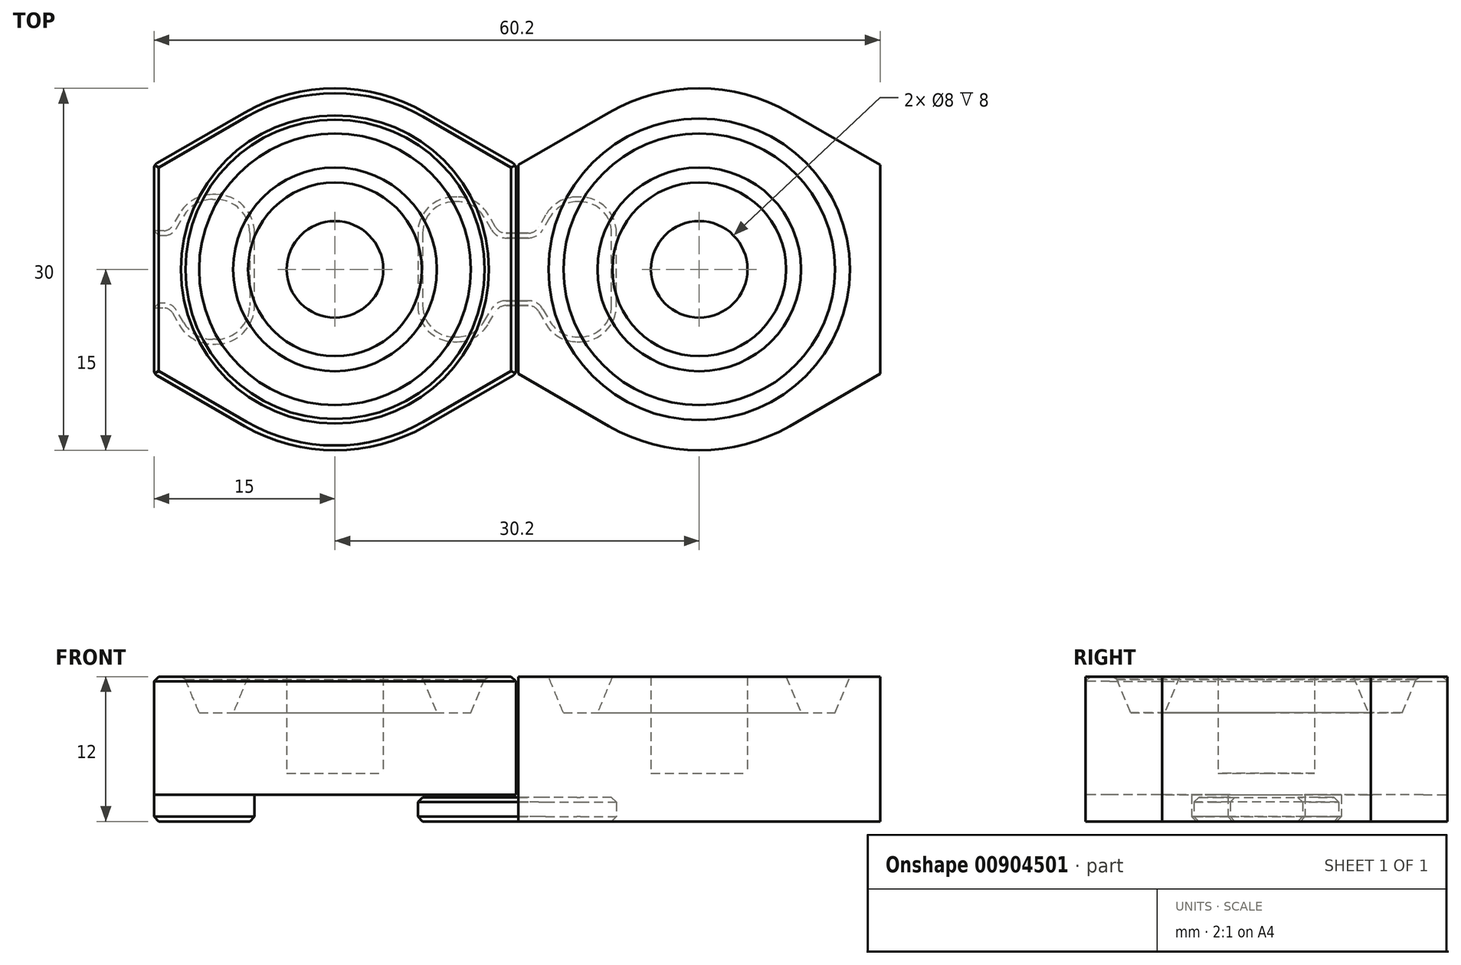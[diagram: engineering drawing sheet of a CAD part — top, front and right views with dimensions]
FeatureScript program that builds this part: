
annotation { "Feature Type Name" : "Feature", "Feature Type Description" : "" }
export const myFeature = defineFeature(function(context is Context, id is Id, definition is map)
    precondition{}
    {
        {
            var Q0;
            Q0=qCreatedBy(makeId("Front.planeOp"),FACE);
            var sketch = newSketch(context, id + "F0", { "sketchPlane" : qUnion([Q0])});
            skLineSegment(sketch, "E0", {"start": v(0, 0) * mm, "end": v(0, 53.45) * mm});
            skLineSegment(sketch, "E1", {"start": v(-4, 12) * mm, "end": v(-7.2, 12) * mm});
            skLineSegment(sketch, "E2", {"start": v(-7.2, 12) * mm, "end": v(-8.44, 9) * mm});
            skLineSegment(sketch, "E3", {"start": v(-8.44, 9) * mm, "end": v(-11.26, 9) * mm});
            skLineSegment(sketch, "E4", {"start": v(-11.26, 9) * mm, "end": v(-12.5, 12) * mm});
            skLineSegment(sketch, "E5", {"start": v(-12.5, 12) * mm, "end": v(-15, 12) * mm});
            skLineSegment(sketch, "E6", {"start": v(-15, 12) * mm, "end": v(-15, 0) * mm});
            skLineSegment(sketch, "E7", {"start": v(-15, 0) * mm, "end": v(0, 0) * mm});
            skLineSegment(sketch, "E8", {"start": v(-4, 12) * mm, "end": v(-4, 0) * mm});
            skLineSegment(sketch, "E9", {"start": v(-9.85, 9) * mm, "end": v(-9.85, 22.32) * mm});
            skLineSegment(sketch, "E10", {"start": v(-4, 4) * mm, "end": v(0, 4) * mm});
            skSolve(sketch);
        }
        {
            var Q0;
            {var subQ4=sQuery(id+"F0.wireOp",EDGE,"E1");Q0=makeQuery(id+"F0.imprint","IMPRINT",FACE,{"disambiguationData":[TD([[makeQuery(id+"F0.imprint","IMPRINT",EDGE,{"derivedFrom":subQ4}),1.0]])]});}
            var Q1;
            {var subQ3=sQuery(id+"F0.wireOp",EDGE,"E10");Q1=makeQuery(id+"F0.imprint","IMPRINT",FACE,{"disambiguationData":[TD([[makeQuery(id+"F0.imprint","IMPRINT",EDGE,{"derivedFrom":subQ3}),-1.0]])]});}
            var Q2;
            Q2=sQuery(id+"F0.wireOp",EDGE,"E0");
            revolve(context, id + "F1", {"surfaceOperationType" : NewSurfaceOperationType.NEW, "entities" : qUnion([Q0, Q1]), "axis" : qUnion([Q2]), "revolveType" : RevolveType.FULL});
        }
        {
            var Q0;
            Q0=qCreatedBy(makeId("Top.planeOp"),FACE);
            var sketch = newSketch(context, id + "F2", { "sketchPlane" : qUnion([Q0])});
            skCircle(sketch, "E11.cCircle", {"center": v(0, 0) * mm, "radius": 15 * mm, "construction": true});
            skLineSegment(sketch, "E11.0", {"start": v(-15, -8.66) * mm, "end": v(-15, 8.66) * mm});
            skLineSegment(sketch, "E11.1", {"start": v(-15, 8.66) * mm, "end": v(0, 17.32) * mm});
            skLineSegment(sketch, "E11.2", {"start": v(0, 17.32) * mm, "end": v(15, 8.66) * mm});
            skLineSegment(sketch, "E11.3", {"start": v(15, 8.66) * mm, "end": v(15, -8.66) * mm});
            skLineSegment(sketch, "E11.4", {"start": v(15, -8.66) * mm, "end": v(0, -17.32) * mm});
            skLineSegment(sketch, "E11.5", {"start": v(0, -17.32) * mm, "end": v(-15, -8.66) * mm});
            skPoint(sketch, "E11.0.midPoint", {"position": v(-15, 0) * mm});
            skCircle(sketch, "E12.0.0", {"center": v(0, 0) * mm, "radius": 15 * mm});
            skSolve(sketch);
        }
        {
            var Q0;
            {var subQ0=sQuery(id+"F2.wireOp",EDGE,"E11.1");var subQ1=sQuery(id+"F2.wireOp",EDGE,"E11.0");var subQ2=makeQuery(id+"F2.imprint","INTERSECT",VERTEX,{"derivedFrom":[subQ1,subQ0]});Q0=makeQuery(id+"F2.imprint","IMPRINT",FACE,{"disambiguationData":[TD([[makeQuery(id+"F2.imprint","IMPRINT",EDGE,{"disambiguationData":[TD([[subQ2,1.0]])],"derivedFrom":subQ1}),-1.0]])]});}
            var Q1;
            {var subQ0=sQuery(id+"F2.wireOp",EDGE,"E11.5");var subQ1=sQuery(id+"F2.wireOp",EDGE,"E11.0");var subQ2=makeQuery(id+"F2.imprint","INTERSECT",VERTEX,{"derivedFrom":[subQ1,subQ0]});Q1=makeQuery(id+"F2.imprint","IMPRINT",FACE,{"disambiguationData":[TD([[makeQuery(id+"F2.imprint","IMPRINT",EDGE,{"disambiguationData":[TD([[subQ2,-1.0]])],"derivedFrom":subQ1}),-1.0]])]});}
            var Q2;
            {var subQ0=sQuery(id+"F2.wireOp",EDGE,"E11.4");var subQ1=sQuery(id+"F2.wireOp",EDGE,"E11.3");var subQ2=makeQuery(id+"F2.imprint","INTERSECT",VERTEX,{"derivedFrom":[subQ1,subQ0]});Q2=makeQuery(id+"F2.imprint","IMPRINT",FACE,{"disambiguationData":[TD([[makeQuery(id+"F2.imprint","IMPRINT",EDGE,{"disambiguationData":[TD([[subQ2,1.0]])],"derivedFrom":subQ1}),-1.0]])]});}
            var Q3;
            {var subQ0=sQuery(id+"F2.wireOp",EDGE,"E11.3");var subQ1=sQuery(id+"F2.wireOp",EDGE,"E11.2");var subQ2=makeQuery(id+"F2.imprint","INTERSECT",VERTEX,{"derivedFrom":[subQ1,subQ0]});Q3=makeQuery(id+"F2.imprint","IMPRINT",FACE,{"disambiguationData":[TD([[makeQuery(id+"F2.imprint","IMPRINT",EDGE,{"disambiguationData":[TD([[subQ2,1.0]])],"derivedFrom":subQ1}),-1.0]])]});}
            var Q4;
            Q4=makeQuery(id+"F1.opRevolve","SWEPT_FACE",FACE,{"disambiguationData":[OSD([sQuery(id+"F0.wireOp",EDGE,"E5")])]});
            extrude(context, id + "F3", {"entities" : qUnion([Q0, Q1, Q2, Q3]), "operationType" : NewBodyOperationType.ADD, "endBound" : BoundingType.UP_TO_SURFACE, "depth" : 25 * mm, "endBoundEntityFace" : qUnion([Q4]), "offsetDistance" : 25 * mm});
        }
        {
            var Q0;
            Q0=makeQuery(id+"F1.opRevolve","SWEPT_BODY",BODY,{"disambiguationData":[OSD([sQuery(id+"F0.wireOp",EDGE,"E0"),sQuery(id+"F0.wireOp",EDGE,"E1"),sQuery(id+"F0.wireOp",EDGE,"E2"),sQuery(id+"F0.wireOp",EDGE,"E3"),sQuery(id+"F0.wireOp",EDGE,"E4"),sQuery(id+"F0.wireOp",EDGE,"E5"),sQuery(id+"F0.wireOp",EDGE,"E6"),sQuery(id+"F0.wireOp",EDGE,"E7"),sQuery(id+"F0.wireOp",EDGE,"E8"),sQuery(id+"F0.wireOp",EDGE,"E10")])]});
            transform(context, id + "F4", {"entities" : qUnion([Q0]), "transformType" : TransformType.TRANSLATION_3D, "dx" : 30.2 * mm, "dy" : 0 * mm, "dz" : 0 * mm, "makeCopy" : true});
        }
        {
            var Q0;
            {var subQ0=sQuery(id+"F2.wireOp",EDGE,"E12.0.0");var subQ1=sQuery(id+"F2.wireOp",EDGE,"E11.3");var subQ2=sQuery(id+"F2.wireOp",EDGE,"E11.0");Q0=makeQuery(id+"F3.boolean.opBoolean","MERGE",FACE,{"derivedFrom":[makeQuery(id+"F1.opRevolve","SWEPT_FACE",FACE,{"disambiguationData":[OSD([sQuery(id+"F0.wireOp",EDGE,"E7")])]}),makeQuery(id+"F3.opExtrude","CAP_FACE",FACE,{"disambiguationData":[OSD([subQ2,sQuery(id+"F2.wireOp",EDGE,"E11.5"),subQ0])],"isStart":true}),makeQuery(id+"F3.opExtrude","CAP_FACE",FACE,{"disambiguationData":[OSD([subQ2,sQuery(id+"F2.wireOp",EDGE,"E11.1"),subQ0])],"isStart":true}),makeQuery(id+"F3.opExtrude","CAP_FACE",FACE,{"disambiguationData":[OSD([sQuery(id+"F2.wireOp",EDGE,"E11.2"),subQ1,subQ0])],"isStart":true}),makeQuery(id+"F3.opExtrude","CAP_FACE",FACE,{"disambiguationData":[OSD([subQ1,sQuery(id+"F2.wireOp",EDGE,"E11.4"),subQ0])],"isStart":true})]});}
            var sketch = newSketch(context, id + "F5", { "sketchPlane" : qUnion([Q0])});
            skLineSegment(sketch, "E13", {"start": v(15, 3) * mm, "end": v(14.18, 3) * mm});
            skLineSegment(sketch, "E14", {"start": v(13.31, 3.5) * mm, "end": v(12.73, 4.5) * mm});
            skLineSegment(sketch, "E15", {"start": v(10.14, 6) * mm, "end": v(9.87, 6) * mm});
            skLineSegment(sketch, "E16", {"start": v(6.87, 3) * mm, "end": v(6.87, -3) * mm});
            skLineSegment(sketch, "E17", {"start": v(9.87, -6) * mm, "end": v(10.14, -6) * mm});
            skLineSegment(sketch, "E18", {"start": v(12.73, -4.5) * mm, "end": v(13.31, -3.5) * mm});
            skLineSegment(sketch, "E19", {"start": v(14.18, -3) * mm, "end": v(15, -3) * mm});
            skLineSegment(sketch, "E20", {"start": v(15, -3) * mm, "end": v(15.1, -3) * mm});
            skLineSegment(sketch, "E21", {"start": v(15.1, -3) * mm, "end": v(15.1, 3) * mm});
            skLineSegment(sketch, "E22", {"start": v(15.1, 3) * mm, "end": v(15, 3) * mm});
            skPoint(sketch, "E23.visualSharp", {"position": v(6.87, 6) * mm});
            skArc(sketch, "E23.filletArc", {"start": v(9.87, 6) * mm, "mid": v(7.75, 5.12) * mm, "end": v(6.87, 3) * mm});
            skPoint(sketch, "E24.visualSharp", {"position": v(6.87, -6) * mm});
            skArc(sketch, "E24.filletArc", {"start": v(6.87, -3) * mm, "mid": v(7.75, -5.12) * mm, "end": v(9.87, -6) * mm});
            skPoint(sketch, "E25.visualSharp", {"position": v(11.87, -6) * mm});
            skArc(sketch, "E25.filletArc", {"start": v(10.14, -6) * mm, "mid": v(11.64, -5.6) * mm, "end": v(12.73, -4.5) * mm});
            skPoint(sketch, "E26.visualSharp", {"position": v(11.87, 6) * mm});
            skArc(sketch, "E26.filletArc", {"start": v(12.73, 4.5) * mm, "mid": v(11.64, 5.6) * mm, "end": v(10.14, 6) * mm});
            skPoint(sketch, "E27.visualSharp", {"position": v(13.6, 3) * mm});
            skArc(sketch, "E27.filletArc", {"start": v(13.31, 3.5) * mm, "mid": v(13.68, 3.13) * mm, "end": v(14.18, 3) * mm});
            skPoint(sketch, "E28.visualSharp", {"position": v(13.6, -3) * mm});
            skArc(sketch, "E28.filletArc", {"start": v(14.18, -3) * mm, "mid": v(13.68, -3.13) * mm, "end": v(13.31, -3.5) * mm});
            skLineSegment(sketch, "E29.MirrorCS", {"start": v(15.1, 3) * mm, "end": v(15.2, 3) * mm});
            skLineSegment(sketch, "E30.MirrorCS", {"start": v(15.2, -3) * mm, "end": v(15.1, -3) * mm});
            skLineSegment(sketch, "E31.MirrorCS", {"start": v(20.33, -6) * mm, "end": v(20.06, -6) * mm});
            skLineSegment(sketch, "E32.MirrorCS", {"start": v(20.06, 6) * mm, "end": v(20.33, 6) * mm});
            skArc(sketch, "E33.MirrorCS", {"start": v(16.89, 3.5) * mm, "mid": v(16.52, 3.13) * mm, "end": v(16.02, 3) * mm});
            skArc(sketch, "E34.MirrorCS", {"start": v(16.02, -3) * mm, "mid": v(16.52, -3.13) * mm, "end": v(16.89, -3.5) * mm});
            skPoint(sketch, "E35.MirrorP", {"position": v(18.33, -6) * mm});
            skLineSegment(sketch, "E36.MirrorCS", {"start": v(16.89, 3.5) * mm, "end": v(17.47, 4.5) * mm});
            skPoint(sketch, "E37.MirrorP", {"position": v(18.33, 6) * mm});
            skPoint(sketch, "E38.MirrorP", {"position": v(23.33, 6) * mm});
            skPoint(sketch, "E39.MirrorP", {"position": v(16.6, -3) * mm});
            skArc(sketch, "E40.MirrorCS", {"start": v(23.33, -3) * mm, "mid": v(22.45, -5.12) * mm, "end": v(20.33, -6) * mm});
            skPoint(sketch, "E41.MirrorP", {"position": v(16.6, 3) * mm});
            skArc(sketch, "E42.MirrorCS", {"start": v(17.47, 4.5) * mm, "mid": v(18.56, 5.6) * mm, "end": v(20.06, 6) * mm});
            skArc(sketch, "E43.MirrorCS", {"start": v(20.33, 6) * mm, "mid": v(22.45, 5.12) * mm, "end": v(23.33, 3) * mm});
            skLineSegment(sketch, "E44.MirrorCS", {"start": v(17.47, -4.5) * mm, "end": v(16.89, -3.5) * mm});
            skLineSegment(sketch, "E45.MirrorCS", {"start": v(23.33, 3) * mm, "end": v(23.33, -3) * mm});
            skLineSegment(sketch, "E46.MirrorCS", {"start": v(15.2, 3) * mm, "end": v(16.02, 3) * mm});
            skPoint(sketch, "E47.MirrorP", {"position": v(23.33, -6) * mm});
            skLineSegment(sketch, "E48.MirrorCS", {"start": v(16.02, -3) * mm, "end": v(15.2, -3) * mm});
            skArc(sketch, "E49.MirrorCS", {"start": v(20.06, -6) * mm, "mid": v(18.56, -5.6) * mm, "end": v(17.47, -4.5) * mm});
            skSolve(sketch);
        }
        {
            var Q0;
            {var subQ1=sQuery(id+"F5.wireOp",EDGE,"E13");Q0=makeQuery(id+"F5.imprint","IMPRINT",FACE,{"disambiguationData":[TD([[makeQuery(id+"F5.imprint","IMPRINT",EDGE,{"derivedFrom":subQ1}),1.0]])]});}
            var Q1;
            {var subQ0=sQuery(id+"F5.wireOp",EDGE,"E20");Q1=makeQuery(id+"F5.imprint","IMPRINT",FACE,{"disambiguationData":[TD([[makeQuery(id+"F5.imprint","IMPRINT",EDGE,{"derivedFrom":subQ0}),1.0]])]});}
            var Q2;
            Q2=makeQuery(id+"F5.imprint","IMPRINT",FACE,{"disambiguationData":[TD([[makeQuery(id+"F5.imprint","IMPRINT",EDGE,{"derivedFrom":sQuery(id+"F5.wireOp",EDGE,"E21")}),-1.0]])]});
            extrude(context, id + "F6", {"entities" : qUnion([Q0, Q1, Q2]), "oppositeDirection" : true, "depth" : 2 * mm, "offsetDistance" : 25 * mm});
        }
        {
            var Q0;
            Q0=makeQuery(id+"F6.opExtrude","SWEPT_BODY",BODY,{"disambiguationData":[OSD([sQuery(id+"F5.wireOp",EDGE,"E13"),sQuery(id+"F5.wireOp",EDGE,"E14"),sQuery(id+"F5.wireOp",EDGE,"E15"),sQuery(id+"F5.wireOp",EDGE,"E16"),sQuery(id+"F5.wireOp",EDGE,"E17"),sQuery(id+"F5.wireOp",EDGE,"E18"),sQuery(id+"F5.wireOp",EDGE,"E19"),sQuery(id+"F5.wireOp",EDGE,"E20"),sQuery(id+"F5.wireOp",EDGE,"E22"),sQuery(id+"F5.wireOp",EDGE,"E23.filletArc"),sQuery(id+"F5.wireOp",EDGE,"E24.filletArc"),sQuery(id+"F5.wireOp",EDGE,"E25.filletArc"),sQuery(id+"F5.wireOp",EDGE,"E26.filletArc"),sQuery(id+"F5.wireOp",EDGE,"E27.filletArc"),sQuery(id+"F5.wireOp",EDGE,"E28.filletArc"),sQuery(id+"F5.wireOp",EDGE,"E29.MirrorCS"),sQuery(id+"F5.wireOp",EDGE,"E30.MirrorCS"),sQuery(id+"F5.wireOp",EDGE,"E31.MirrorCS"),sQuery(id+"F5.wireOp",EDGE,"E32.MirrorCS"),sQuery(id+"F5.wireOp",EDGE,"E33.MirrorCS"),sQuery(id+"F5.wireOp",EDGE,"E34.MirrorCS"),sQuery(id+"F5.wireOp",EDGE,"E36.MirrorCS"),sQuery(id+"F5.wireOp",EDGE,"E40.MirrorCS"),sQuery(id+"F5.wireOp",EDGE,"E42.MirrorCS"),sQuery(id+"F5.wireOp",EDGE,"E43.MirrorCS"),sQuery(id+"F5.wireOp",EDGE,"E44.MirrorCS"),sQuery(id+"F5.wireOp",EDGE,"E45.MirrorCS"),sQuery(id+"F5.wireOp",EDGE,"E46.MirrorCS"),sQuery(id+"F5.wireOp",EDGE,"E48.MirrorCS"),sQuery(id+"F5.wireOp",EDGE,"E49.MirrorCS")])]});
            var Q1;
            Q1=makeQuery(id+"F1.opRevolve","SWEPT_BODY",BODY,{"disambiguationData":[OSD([sQuery(id+"F0.wireOp",EDGE,"E0"),sQuery(id+"F0.wireOp",EDGE,"E1"),sQuery(id+"F0.wireOp",EDGE,"E2"),sQuery(id+"F0.wireOp",EDGE,"E3"),sQuery(id+"F0.wireOp",EDGE,"E4"),sQuery(id+"F0.wireOp",EDGE,"E5"),sQuery(id+"F0.wireOp",EDGE,"E6"),sQuery(id+"F0.wireOp",EDGE,"E7"),sQuery(id+"F0.wireOp",EDGE,"E8"),sQuery(id+"F0.wireOp",EDGE,"E10")])]});
            booleanBodies(context, id + "F7", {"operationType" : BooleanOperationType.SUBTRACTION, "tools" : qUnion([Q0]), "targets" : qUnion([Q1]), "offset" : true, "offsetAll" : true, "offsetDistance" : .2 * mm, "keepTools" : true});
        }
        {
            var Q0;
            {var subQ0=sQuery(id+"F2.wireOp",EDGE,"E12.0.0");var subQ1=sQuery(id+"F2.wireOp",EDGE,"E11.3");var subQ2=sQuery(id+"F2.wireOp",EDGE,"E11.0");Q0=makeQuery(id+"F3.boolean.opBoolean","MERGE",FACE,{"derivedFrom":[makeQuery(id+"F1.opRevolve","SWEPT_FACE",FACE,{"disambiguationData":[OSD([sQuery(id+"F0.wireOp",EDGE,"E7")])]}),makeQuery(id+"F3.opExtrude","CAP_FACE",FACE,{"disambiguationData":[OSD([subQ2,sQuery(id+"F2.wireOp",EDGE,"E11.5"),subQ0])],"isStart":true}),makeQuery(id+"F3.opExtrude","CAP_FACE",FACE,{"disambiguationData":[OSD([subQ2,sQuery(id+"F2.wireOp",EDGE,"E11.1"),subQ0])],"isStart":true}),makeQuery(id+"F3.opExtrude","CAP_FACE",FACE,{"disambiguationData":[OSD([sQuery(id+"F2.wireOp",EDGE,"E11.2"),subQ1,subQ0])],"isStart":true}),makeQuery(id+"F3.opExtrude","CAP_FACE",FACE,{"disambiguationData":[OSD([subQ1,sQuery(id+"F2.wireOp",EDGE,"E11.4"),subQ0])],"isStart":true})]});}
            var sketch = newSketch(context, id + "F8", { "sketchPlane" : qUnion([Q0])});
            skLineSegment(sketch, "E50.0.0", {"start": v(15, -8.66) * mm, "end": v(15, -3.2) * mm});
            skLineSegment(sketch, "E50.0.1", {"start": v(15, -3.2) * mm, "end": v(14.18, -3.2) * mm});
            skArc(sketch, "E50.0.2", {"start": v(14.18, -3.2) * mm, "mid": v(13.78, -3.3) * mm, "end": v(13.48, -3.6) * mm});
            skLineSegment(sketch, "E50.0.3", {"start": v(13.48, -3.6) * mm, "end": v(12.9, -4.6) * mm});
            skArc(sketch, "E50.0.4", {"start": v(12.9, -4.6) * mm, "mid": v(11.74, -5.77) * mm, "end": v(10.14, -6.2) * mm});
            skLineSegment(sketch, "E50.0.5", {"start": v(10.14, -6.2) * mm, "end": v(9.87, -6.2) * mm});
            skArc(sketch, "E50.0.6", {"start": v(9.87, -6.2) * mm, "mid": v(7.6, -5.26) * mm, "end": v(6.67, -3) * mm});
            skLineSegment(sketch, "E50.0.7", {"start": v(6.67, -3) * mm, "end": v(6.67, 3) * mm});
            skArc(sketch, "E50.0.8", {"start": v(6.67, 3) * mm, "mid": v(7.6, 5.26) * mm, "end": v(9.87, 6.2) * mm});
            skLineSegment(sketch, "E50.0.9", {"start": v(9.87, 6.2) * mm, "end": v(10.14, 6.2) * mm});
            skArc(sketch, "E50.0.10", {"start": v(10.14, 6.2) * mm, "mid": v(11.74, 5.77) * mm, "end": v(12.9, 4.6) * mm});
            skLineSegment(sketch, "E50.0.11", {"start": v(12.9, 4.6) * mm, "end": v(13.48, 3.6) * mm});
            skArc(sketch, "E50.0.12", {"start": v(13.48, 3.6) * mm, "mid": v(13.78, 3.3) * mm, "end": v(14.18, 3.2) * mm});
            skLineSegment(sketch, "E50.0.13", {"start": v(14.18, 3.2) * mm, "end": v(15, 3.2) * mm});
            skLineSegment(sketch, "E50.0.14", {"start": v(15, 3.2) * mm, "end": v(15, 8.66) * mm});
            skLineSegment(sketch, "E50.0.15", {"start": v(15, 8.66) * mm, "end": v(7.5, 13) * mm});
            skArc(sketch, "E50.0.16", {"start": v(7.5, 13) * mm, "mid": v(0, 15) * mm, "end": v(-7.5, 13) * mm});
            skLineSegment(sketch, "E50.0.17", {"start": v(-7.5, 13) * mm, "end": v(-15, 8.66) * mm});
            skLineSegment(sketch, "E50.0.18", {"start": v(-15, 8.66) * mm, "end": v(-15, -8.66) * mm});
            skLineSegment(sketch, "E50.0.19", {"start": v(-15, -8.66) * mm, "end": v(-7.5, -13) * mm});
            skArc(sketch, "E50.0.20", {"start": v(-7.5, -13) * mm, "mid": v(0, -15) * mm, "end": v(7.5, -13) * mm});
            skLineSegment(sketch, "E50.0.21", {"start": v(7.5, -13) * mm, "end": v(15, -8.66) * mm});
            skArc(sketch, "E51.MirrorCS", {"start": v(-14.18, -3.2) * mm, "mid": v(-13.78, -3.3) * mm, "end": v(-13.48, -3.6) * mm});
            skLineSegment(sketch, "E52.MirrorCS", {"start": v(-15, -3.2) * mm, "end": v(-14.18, -3.2) * mm});
            skArc(sketch, "E53.MirrorCS", {"start": v(-13.48, 3.6) * mm, "mid": v(-13.78, 3.3) * mm, "end": v(-14.18, 3.2) * mm});
            skLineSegment(sketch, "E54.MirrorCS", {"start": v(-12.9, 4.6) * mm, "end": v(-13.48, 3.6) * mm});
            skLineSegment(sketch, "E55.MirrorCS", {"start": v(-14.18, 3.2) * mm, "end": v(-15, 3.2) * mm});
            skLineSegment(sketch, "E56.MirrorCS", {"start": v(-9.87, 6.2) * mm, "end": v(-10.14, 6.2) * mm});
            skLineSegment(sketch, "E57.MirrorCS", {"start": v(-10.14, -6.2) * mm, "end": v(-9.87, -6.2) * mm});
            skLineSegment(sketch, "E58.MirrorCS", {"start": v(-13.48, -3.6) * mm, "end": v(-12.9, -4.6) * mm});
            skArc(sketch, "E59.MirrorCS", {"start": v(-10.14, 6.2) * mm, "mid": v(-11.74, 5.77) * mm, "end": v(-12.9, 4.6) * mm});
            skArc(sketch, "E60.MirrorCS", {"start": v(-6.67, 3) * mm, "mid": v(-7.6, 5.26) * mm, "end": v(-9.87, 6.2) * mm});
            skLineSegment(sketch, "E61.MirrorCS", {"start": v(-6.67, -3) * mm, "end": v(-6.67, 3) * mm});
            skArc(sketch, "E62.MirrorCS", {"start": v(-9.87, -6.2) * mm, "mid": v(-7.6, -5.26) * mm, "end": v(-6.67, -3) * mm});
            skArc(sketch, "E63.MirrorCS", {"start": v(-12.9, -4.6) * mm, "mid": v(-11.74, -5.77) * mm, "end": v(-10.14, -6.2) * mm});
            skSolve(sketch);
        }
        {
            var Q0;
            Q0=makeQuery(id+"F8.imprint","IMPRINT",FACE,{"disambiguationData":[TD([[makeQuery(id+"F8.imprint","IMPRINT",EDGE,{"derivedFrom":sQuery(id+"F8.wireOp",EDGE,"E51.MirrorCS")}),1.0]])]});
            var Q1;
            Q1=makeQuery(id+"F7.tempBoolean.opBoolean","COPY",FACE,{"derivedFrom":makeQuery(id+"F7.offsetTempBody.opPattern","COPY",FACE,{"derivedFrom":makeQuery(id+"F6.opExtrude","CAP_FACE",FACE,{"disambiguationData":[OSD([sQuery(id+"F5.wireOp",EDGE,"E13"),sQuery(id+"F5.wireOp",EDGE,"E14"),sQuery(id+"F5.wireOp",EDGE,"E15"),sQuery(id+"F5.wireOp",EDGE,"E16"),sQuery(id+"F5.wireOp",EDGE,"E17"),sQuery(id+"F5.wireOp",EDGE,"E18"),sQuery(id+"F5.wireOp",EDGE,"E19"),sQuery(id+"F5.wireOp",EDGE,"E20"),sQuery(id+"F5.wireOp",EDGE,"E22"),sQuery(id+"F5.wireOp",EDGE,"E23.filletArc"),sQuery(id+"F5.wireOp",EDGE,"E24.filletArc"),sQuery(id+"F5.wireOp",EDGE,"E25.filletArc"),sQuery(id+"F5.wireOp",EDGE,"E26.filletArc"),sQuery(id+"F5.wireOp",EDGE,"E27.filletArc"),sQuery(id+"F5.wireOp",EDGE,"E28.filletArc"),sQuery(id+"F5.wireOp",EDGE,"E29.MirrorCS"),sQuery(id+"F5.wireOp",EDGE,"E30.MirrorCS"),sQuery(id+"F5.wireOp",EDGE,"E31.MirrorCS"),sQuery(id+"F5.wireOp",EDGE,"E32.MirrorCS"),sQuery(id+"F5.wireOp",EDGE,"E33.MirrorCS"),sQuery(id+"F5.wireOp",EDGE,"E34.MirrorCS"),sQuery(id+"F5.wireOp",EDGE,"E36.MirrorCS"),sQuery(id+"F5.wireOp",EDGE,"E40.MirrorCS"),sQuery(id+"F5.wireOp",EDGE,"E42.MirrorCS"),sQuery(id+"F5.wireOp",EDGE,"E43.MirrorCS"),sQuery(id+"F5.wireOp",EDGE,"E44.MirrorCS"),sQuery(id+"F5.wireOp",EDGE,"E45.MirrorCS"),sQuery(id+"F5.wireOp",EDGE,"E46.MirrorCS"),sQuery(id+"F5.wireOp",EDGE,"E48.MirrorCS"),sQuery(id+"F5.wireOp",EDGE,"E49.MirrorCS")])],"isStart":false}),"instanceName":"1"})});
            extrude(context, id + "F9", {"entities" : qUnion([Q0]), "operationType" : NewBodyOperationType.REMOVE, "endBound" : BoundingType.UP_TO_SURFACE, "oppositeDirection" : true, "depth" : 25 * mm, "endBoundEntityFace" : qUnion([Q1]), "offsetDistance" : 25 * mm});
        }
        {
            var Q0;
            {var subQ0=sQuery(id+"F2.wireOp",EDGE,"E12.0.0");var subQ1=sQuery(id+"F2.wireOp",EDGE,"E11.3");var subQ2=sQuery(id+"F2.wireOp",EDGE,"E11.0");Q0=makeQuery(id+"F3.boolean.opBoolean","MERGE",FACE,{"derivedFrom":[makeQuery(id+"F1.opRevolve","SWEPT_FACE",FACE,{"disambiguationData":[OSD([sQuery(id+"F0.wireOp",EDGE,"E7")])]}),makeQuery(id+"F3.opExtrude","CAP_FACE",FACE,{"disambiguationData":[OSD([subQ2,sQuery(id+"F2.wireOp",EDGE,"E11.5"),subQ0])],"isStart":true}),makeQuery(id+"F3.opExtrude","CAP_FACE",FACE,{"disambiguationData":[OSD([subQ2,sQuery(id+"F2.wireOp",EDGE,"E11.1"),subQ0])],"isStart":true}),makeQuery(id+"F3.opExtrude","CAP_FACE",FACE,{"disambiguationData":[OSD([sQuery(id+"F2.wireOp",EDGE,"E11.2"),subQ1,subQ0])],"isStart":true}),makeQuery(id+"F3.opExtrude","CAP_FACE",FACE,{"disambiguationData":[OSD([subQ1,sQuery(id+"F2.wireOp",EDGE,"E11.4"),subQ0])],"isStart":true})]});}
            chamfer(context, id + "F10", {"entities" : qUnion([Q0]), "width" : .4 * mm, "tangentPropagation" : true});
        }
        {
            var Q0;
            {var subQ0=sQuery(id+"F2.wireOp",EDGE,"E12.0.0");var subQ1=sQuery(id+"F2.wireOp",EDGE,"E11.3");var subQ2=sQuery(id+"F2.wireOp",EDGE,"E11.0");Q0=makeQuery(id+"F3.boolean.opBoolean","MERGE",FACE,{"derivedFrom":[makeQuery(id+"F1.opRevolve","SWEPT_FACE",FACE,{"disambiguationData":[OSD([sQuery(id+"F0.wireOp",EDGE,"E5")])]}),makeQuery(id+"F3.opExtrude","CAP_FACE",FACE,{"disambiguationData":[OSD([subQ2,sQuery(id+"F2.wireOp",EDGE,"E11.5"),subQ0])],"isStart":false}),makeQuery(id+"F3.opExtrude","CAP_FACE",FACE,{"disambiguationData":[OSD([subQ2,sQuery(id+"F2.wireOp",EDGE,"E11.1"),subQ0])],"isStart":false}),makeQuery(id+"F3.opExtrude","CAP_FACE",FACE,{"disambiguationData":[OSD([sQuery(id+"F2.wireOp",EDGE,"E11.2"),subQ1,subQ0])],"isStart":false}),makeQuery(id+"F3.opExtrude","CAP_FACE",FACE,{"disambiguationData":[OSD([subQ1,sQuery(id+"F2.wireOp",EDGE,"E11.4"),subQ0])],"isStart":false})]});}
            chamfer(context, id + "F11", {"entities" : qUnion([Q0]), "width" : .4 * mm, "tangentPropagation" : true});
        }
        {
            var Q0;
            Q0=makeQuery(id+"F3.opExtrude","SWEPT_EDGE",EDGE,{"disambiguationData":[OSD([sQuery(id+"F2.wireOp",EDGE,"E11.3"),sQuery(id+"F2.wireOp",EDGE,"E11.4")])]});
            var Q1;
            Q1=makeQuery(id+"F3.opExtrude","SWEPT_EDGE",EDGE,{"disambiguationData":[OSD([sQuery(id+"F2.wireOp",EDGE,"E11.2"),sQuery(id+"F2.wireOp",EDGE,"E11.3")])]});
            var Q2;
            Q2=makeQuery(id+"F3.opExtrude","SWEPT_EDGE",EDGE,{"disambiguationData":[OSD([sQuery(id+"F2.wireOp",EDGE,"E11.0"),sQuery(id+"F2.wireOp",EDGE,"E11.5")])]});
            var Q3;
            Q3=makeQuery(id+"F3.opExtrude","SWEPT_EDGE",EDGE,{"disambiguationData":[OSD([sQuery(id+"F2.wireOp",EDGE,"E11.0"),sQuery(id+"F2.wireOp",EDGE,"E11.1")])]});
            var Q4;
            Q4=makeQuery(id+"F9.boolean.opBoolean","COPY",EDGE,{"derivedFrom":makeQuery(id+"F9.opExtrude","SWEPT_EDGE",EDGE,{"disambiguationData":[OSD([sQuery(id+"F8.wireOp",EDGE,"E50.0.18"),sQuery(id+"F8.wireOp",EDGE,"E52.MirrorCS")])]})});
            var Q5;
            Q5=makeQuery(id+"F9.boolean.opBoolean","COPY",EDGE,{"derivedFrom":makeQuery(id+"F9.opExtrude","SWEPT_EDGE",EDGE,{"disambiguationData":[OSD([sQuery(id+"F8.wireOp",EDGE,"E50.0.18"),sQuery(id+"F8.wireOp",EDGE,"E55.MirrorCS")])]})});
            var Q6;
            {var subQ0=sQuery(id+"F2.wireOp",EDGE,"E11.3");Q6=makeQuery(id+"F7.tempBoolean.opBoolean","INTERSECT",EDGE,{"derivedFrom":[makeQuery(id+"F3.boolean.opBoolean","MERGE",FACE,{"derivedFrom":[makeQuery(id+"F3.opExtrude","SWEPT_FACE",FACE,{"disambiguationData":[OSD([subQ0]),TDD([makeQuery(id+"F2.imprint","IMPRINT",EDGE,{"disambiguationData":[TD([[makeQuery(id+"F2.imprint","INTERSECT",VERTEX,{"derivedFrom":[sQuery(id+"F2.wireOp",EDGE,"E11.2"),subQ0]}),-1.0]])],"derivedFrom":subQ0})])]}),makeQuery(id+"F3.opExtrude","SWEPT_FACE",FACE,{"disambiguationData":[OSD([subQ0]),TDD([makeQuery(id+"F2.imprint","IMPRINT",EDGE,{"disambiguationData":[TD([[makeQuery(id+"F2.imprint","INTERSECT",VERTEX,{"derivedFrom":[subQ0,sQuery(id+"F2.wireOp",EDGE,"E11.4")]}),1.0]])],"derivedFrom":subQ0})])]})]}),makeQuery(id+"F7.offsetTempBody.opPattern","COPY",FACE,{"derivedFrom":makeQuery(id+"F6.opExtrude","SWEPT_FACE",FACE,{"disambiguationData":[OSD([sQuery(id+"F5.wireOp",EDGE,"E13"),sQuery(id+"F5.wireOp",EDGE,"E22"),sQuery(id+"F5.wireOp",EDGE,"E29.MirrorCS"),sQuery(id+"F5.wireOp",EDGE,"E46.MirrorCS")])]}),"instanceName":"1"})]});}
            var Q7;
            {var subQ0=sQuery(id+"F2.wireOp",EDGE,"E11.3");Q7=makeQuery(id+"F7.tempBoolean.opBoolean","INTERSECT",EDGE,{"derivedFrom":[makeQuery(id+"F3.boolean.opBoolean","MERGE",FACE,{"derivedFrom":[makeQuery(id+"F3.opExtrude","SWEPT_FACE",FACE,{"disambiguationData":[OSD([subQ0]),TDD([makeQuery(id+"F2.imprint","IMPRINT",EDGE,{"disambiguationData":[TD([[makeQuery(id+"F2.imprint","INTERSECT",VERTEX,{"derivedFrom":[sQuery(id+"F2.wireOp",EDGE,"E11.2"),subQ0]}),-1.0]])],"derivedFrom":subQ0})])]}),makeQuery(id+"F3.opExtrude","SWEPT_FACE",FACE,{"disambiguationData":[OSD([subQ0]),TDD([makeQuery(id+"F2.imprint","IMPRINT",EDGE,{"disambiguationData":[TD([[makeQuery(id+"F2.imprint","INTERSECT",VERTEX,{"derivedFrom":[subQ0,sQuery(id+"F2.wireOp",EDGE,"E11.4")]}),1.0]])],"derivedFrom":subQ0})])]})]}),makeQuery(id+"F7.offsetTempBody.opPattern","COPY",FACE,{"derivedFrom":makeQuery(id+"F6.opExtrude","SWEPT_FACE",FACE,{"disambiguationData":[OSD([sQuery(id+"F5.wireOp",EDGE,"E19"),sQuery(id+"F5.wireOp",EDGE,"E20"),sQuery(id+"F5.wireOp",EDGE,"E30.MirrorCS"),sQuery(id+"F5.wireOp",EDGE,"E48.MirrorCS")])]}),"instanceName":"1"})]});}
            fillet(context, id + "F12", {"entities" : qUnion([Q0, Q1, Q2, Q3, Q4, Q5, Q6, Q7]), "radius" : .5 * mm, "tangentPropagation" : true, "allowEdgeOverflow" : false});
        }
        {
            var Q0;
            Q0=makeQuery(id+"F6.opExtrude","CAP_FACE",FACE,{"disambiguationData":[OSD([sQuery(id+"F5.wireOp",EDGE,"E13"),sQuery(id+"F5.wireOp",EDGE,"E14"),sQuery(id+"F5.wireOp",EDGE,"E15"),sQuery(id+"F5.wireOp",EDGE,"E16"),sQuery(id+"F5.wireOp",EDGE,"E17"),sQuery(id+"F5.wireOp",EDGE,"E18"),sQuery(id+"F5.wireOp",EDGE,"E19"),sQuery(id+"F5.wireOp",EDGE,"E20"),sQuery(id+"F5.wireOp",EDGE,"E22"),sQuery(id+"F5.wireOp",EDGE,"E23.filletArc"),sQuery(id+"F5.wireOp",EDGE,"E24.filletArc"),sQuery(id+"F5.wireOp",EDGE,"E25.filletArc"),sQuery(id+"F5.wireOp",EDGE,"E26.filletArc"),sQuery(id+"F5.wireOp",EDGE,"E27.filletArc"),sQuery(id+"F5.wireOp",EDGE,"E28.filletArc"),sQuery(id+"F5.wireOp",EDGE,"E29.MirrorCS"),sQuery(id+"F5.wireOp",EDGE,"E30.MirrorCS"),sQuery(id+"F5.wireOp",EDGE,"E31.MirrorCS"),sQuery(id+"F5.wireOp",EDGE,"E32.MirrorCS"),sQuery(id+"F5.wireOp",EDGE,"E33.MirrorCS"),sQuery(id+"F5.wireOp",EDGE,"E34.MirrorCS"),sQuery(id+"F5.wireOp",EDGE,"E36.MirrorCS"),sQuery(id+"F5.wireOp",EDGE,"E40.MirrorCS"),sQuery(id+"F5.wireOp",EDGE,"E42.MirrorCS"),sQuery(id+"F5.wireOp",EDGE,"E43.MirrorCS"),sQuery(id+"F5.wireOp",EDGE,"E44.MirrorCS"),sQuery(id+"F5.wireOp",EDGE,"E45.MirrorCS"),sQuery(id+"F5.wireOp",EDGE,"E46.MirrorCS"),sQuery(id+"F5.wireOp",EDGE,"E48.MirrorCS"),sQuery(id+"F5.wireOp",EDGE,"E49.MirrorCS")])],"isStart":false});
            var Q1;
            Q1=makeQuery(id+"F6.opExtrude","CAP_FACE",FACE,{"disambiguationData":[OSD([sQuery(id+"F5.wireOp",EDGE,"E13"),sQuery(id+"F5.wireOp",EDGE,"E14"),sQuery(id+"F5.wireOp",EDGE,"E15"),sQuery(id+"F5.wireOp",EDGE,"E16"),sQuery(id+"F5.wireOp",EDGE,"E17"),sQuery(id+"F5.wireOp",EDGE,"E18"),sQuery(id+"F5.wireOp",EDGE,"E19"),sQuery(id+"F5.wireOp",EDGE,"E20"),sQuery(id+"F5.wireOp",EDGE,"E22"),sQuery(id+"F5.wireOp",EDGE,"E23.filletArc"),sQuery(id+"F5.wireOp",EDGE,"E24.filletArc"),sQuery(id+"F5.wireOp",EDGE,"E25.filletArc"),sQuery(id+"F5.wireOp",EDGE,"E26.filletArc"),sQuery(id+"F5.wireOp",EDGE,"E27.filletArc"),sQuery(id+"F5.wireOp",EDGE,"E28.filletArc"),sQuery(id+"F5.wireOp",EDGE,"E29.MirrorCS"),sQuery(id+"F5.wireOp",EDGE,"E30.MirrorCS"),sQuery(id+"F5.wireOp",EDGE,"E31.MirrorCS"),sQuery(id+"F5.wireOp",EDGE,"E32.MirrorCS"),sQuery(id+"F5.wireOp",EDGE,"E33.MirrorCS"),sQuery(id+"F5.wireOp",EDGE,"E34.MirrorCS"),sQuery(id+"F5.wireOp",EDGE,"E36.MirrorCS"),sQuery(id+"F5.wireOp",EDGE,"E40.MirrorCS"),sQuery(id+"F5.wireOp",EDGE,"E42.MirrorCS"),sQuery(id+"F5.wireOp",EDGE,"E43.MirrorCS"),sQuery(id+"F5.wireOp",EDGE,"E44.MirrorCS"),sQuery(id+"F5.wireOp",EDGE,"E45.MirrorCS"),sQuery(id+"F5.wireOp",EDGE,"E46.MirrorCS"),sQuery(id+"F5.wireOp",EDGE,"E48.MirrorCS"),sQuery(id+"F5.wireOp",EDGE,"E49.MirrorCS")])],"isStart":true});
            chamfer(context, id + "F13", {"entities" : qUnion([Q0, Q1]), "width" : .4 * mm, "tangentPropagation" : true});
        }
    });
